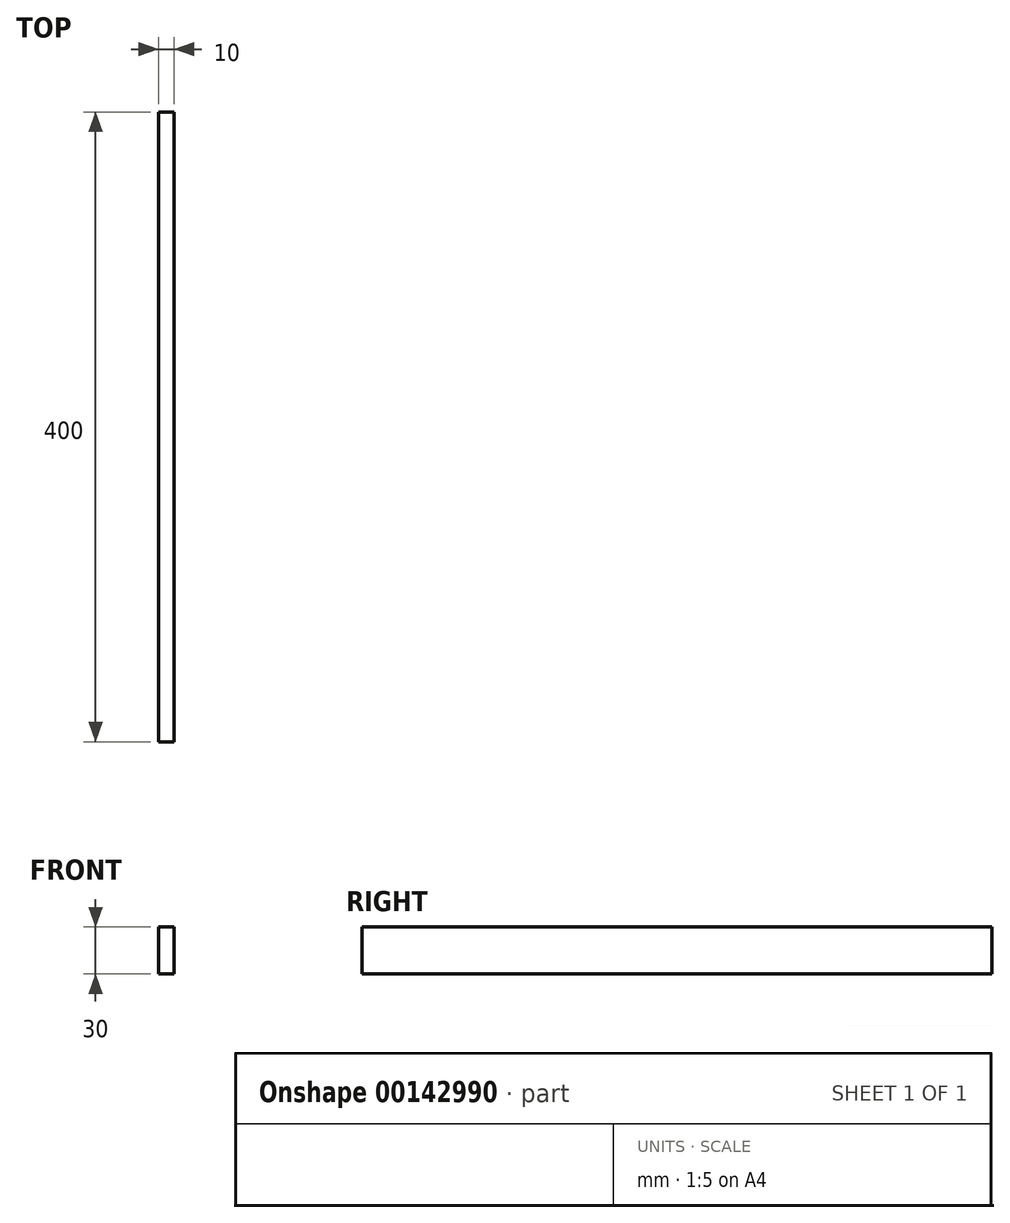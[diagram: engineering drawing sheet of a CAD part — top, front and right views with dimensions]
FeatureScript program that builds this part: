
annotation { "Feature Type Name" : "Feature", "Feature Type Description" : "" }
export const myFeature = defineFeature(function(context is Context, id is Id, definition is map)
    precondition{}
    {
        {
            var Q0;
            Q0=qCreatedBy(makeId("Right.planeOp"),FACE);
            var sketch = newSketch(context, id + "F0", { "sketchPlane" : qUnion([Q0])});
            skLineSegment(sketch, "E0.bottom", {"start": v(0, 0) * mm, "end": v(400, 0) * mm});
            skLineSegment(sketch, "E0.top", {"start": v(0, 30) * mm, "end": v(400, 30) * mm});
            skLineSegment(sketch, "E0.left", {"start": v(0, 0) * mm, "end": v(0, 30) * mm});
            skLineSegment(sketch, "E0.right", {"start": v(400, 0) * mm, "end": v(400, 30) * mm});
            skSolve(sketch);
        }
        {
            var Q0;
            Q0 = qSketchRegion(id + "F0", true);
            extrude(context, id + "F1", {"entities" : qUnion([Q0]), "depth" : 10 * mm, "offsetDistance" : 25 * mm});
        }
    });
